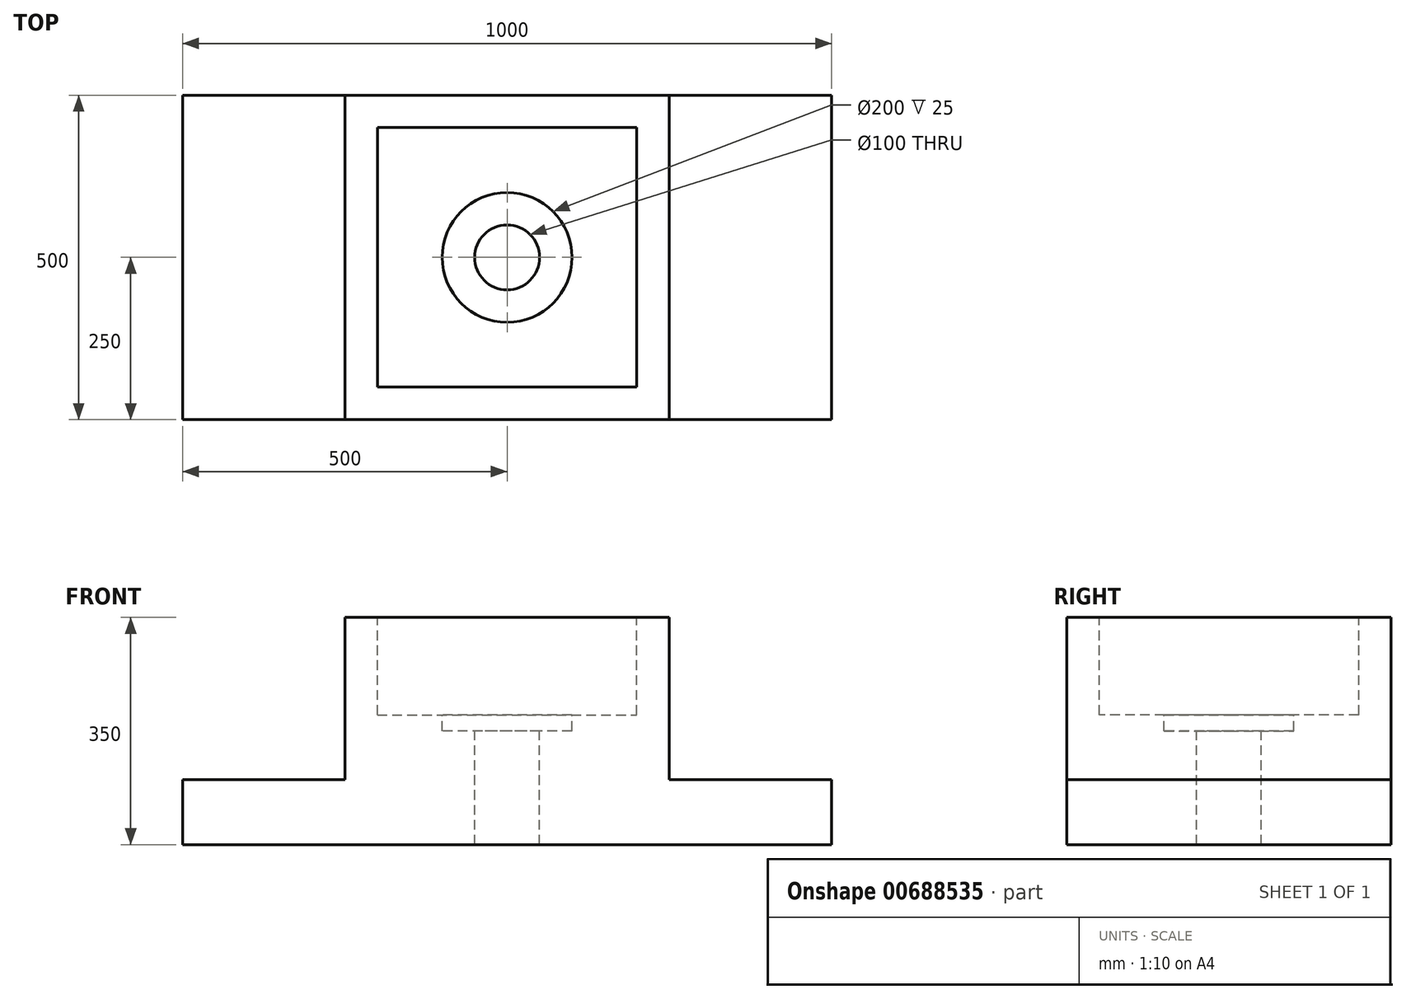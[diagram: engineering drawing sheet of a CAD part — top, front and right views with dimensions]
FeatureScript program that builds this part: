
annotation { "Feature Type Name" : "Feature", "Feature Type Description" : "" }
export const myFeature = defineFeature(function(context is Context, id is Id, definition is map)
    precondition{}
    {
        {
            var Q0;
            Q0=qCreatedBy(makeId("Front.planeOp"),FACE);
            var sketch = newSketch(context, id + "F0", { "sketchPlane" : qUnion([Q0])});
            skLineSegment(sketch, "E0", {"start": v(0, 0) * mm, "end": v(-1000, 0) * mm});
            skLineSegment(sketch, "E1", {"start": v(-1000, 0) * mm, "end": v(-1000, 100) * mm});
            skLineSegment(sketch, "E2", {"start": v(-1000, 100) * mm, "end": v(-750, 100) * mm});
            skLineSegment(sketch, "E3", {"start": v(-750, 100) * mm, "end": v(-750, 350) * mm});
            skLineSegment(sketch, "E4", {"start": v(-750, 350) * mm, "end": v(-250, 350) * mm});
            skLineSegment(sketch, "E5", {"start": v(-250, 350) * mm, "end": v(-250, 100) * mm});
            skLineSegment(sketch, "E6", {"start": v(-250, 100) * mm, "end": v(0, 100) * mm});
            skLineSegment(sketch, "E7", {"start": v(0, 100) * mm, "end": v(0, 0) * mm});
            skSolve(sketch);
        }
        {
            var Q0;
            Q0 = qSketchRegion(id + "F0", true);
            extrude(context, id + "F1", {"entities" : qUnion([Q0]), "depth" : 500 * mm, "offsetDistance" : 25 * mm});
        }
        {
            var Q0;
            Q0=makeQuery(id+"F1.opExtrude","SWEPT_FACE",FACE,{"disambiguationData":[OSD([sQuery(id+"F0.wireOp",EDGE,"E4")])]});
            var sketch = newSketch(context, id + "F2", { "sketchPlane" : qUnion([Q0])});
            skLineSegment(sketch, "E8.bottom", {"start": v(-700, -50) * mm, "end": v(-300, -50) * mm});
            skLineSegment(sketch, "E8.top", {"start": v(-700, -450) * mm, "end": v(-300, -450) * mm});
            skLineSegment(sketch, "E8.left", {"start": v(-700, -50) * mm, "end": v(-700, -450) * mm});
            skLineSegment(sketch, "E8.right", {"start": v(-300, -50) * mm, "end": v(-300, -450) * mm});
            skSolve(sketch);
        }
        {
            var Q0;
            Q0 = qSketchRegion(id + "F2", true);
            extrude(context, id + "F3", {"entities" : qUnion([Q0]), "operationType" : NewBodyOperationType.REMOVE, "oppositeDirection" : true, "depth" : 150 * mm, "offsetDistance" : 25 * mm});
        }
        {
            var Q0;
            Q0=makeQuery(id+"F3.boolean.opBoolean","COPY",FACE,{"derivedFrom":makeQuery(id+"F3.opExtrude","CAP_FACE",FACE,{"disambiguationData":[OSD([sQuery(id+"F2.wireOp",EDGE,"E8.bottom"),sQuery(id+"F2.wireOp",EDGE,"E8.top"),sQuery(id+"F2.wireOp",EDGE,"E8.left"),sQuery(id+"F2.wireOp",EDGE,"E8.right")])],"isStart":false})});
            var sketch = newSketch(context, id + "F4", { "sketchPlane" : qUnion([Q0])});
            skCircle(sketch, "E9", {"center": v(-500, -250) * mm, "radius": 100 * mm});
            skPoint(sketch, "E9.centerSnap0", {"position": v(-700, -250) * mm});
            skPoint(sketch, "E9.centerSnap1", {"position": v(-500, -50) * mm});
            skCircle(sketch, "E10", {"center": v(-500, -250) * mm, "radius": 50 * mm});
            skSolve(sketch);
        }
        {
            var Q0;
            Q0=makeQuery(id+"F4.imprint","IMPRINT",FACE,{"disambiguationData":[TD([[makeQuery(id+"F4.imprint","IMPRINT",EDGE,{"derivedFrom":sQuery(id+"F4.wireOp",EDGE,"E9")}),1.0]])]});
            extrude(context, id + "F5", {"entities" : qUnion([Q0]), "operationType" : NewBodyOperationType.REMOVE, "oppositeDirection" : true, "depth" : 25 * mm, "offsetDistance" : 25 * mm});
        }
        {
            var Q0;
            Q0=makeQuery(id+"F4.imprint","IMPRINT",FACE,{"disambiguationData":[TD([[makeQuery(id+"F4.imprint","IMPRINT",EDGE,{"derivedFrom":sQuery(id+"F4.wireOp",EDGE,"E10")}),1.0]])]});
            extrude(context, id + "F6", {"entities" : qUnion([Q0]), "operationType" : NewBodyOperationType.REMOVE, "oppositeDirection" : true, "depth" : 200 * mm, "offsetDistance" : 25 * mm});
        }
    });
